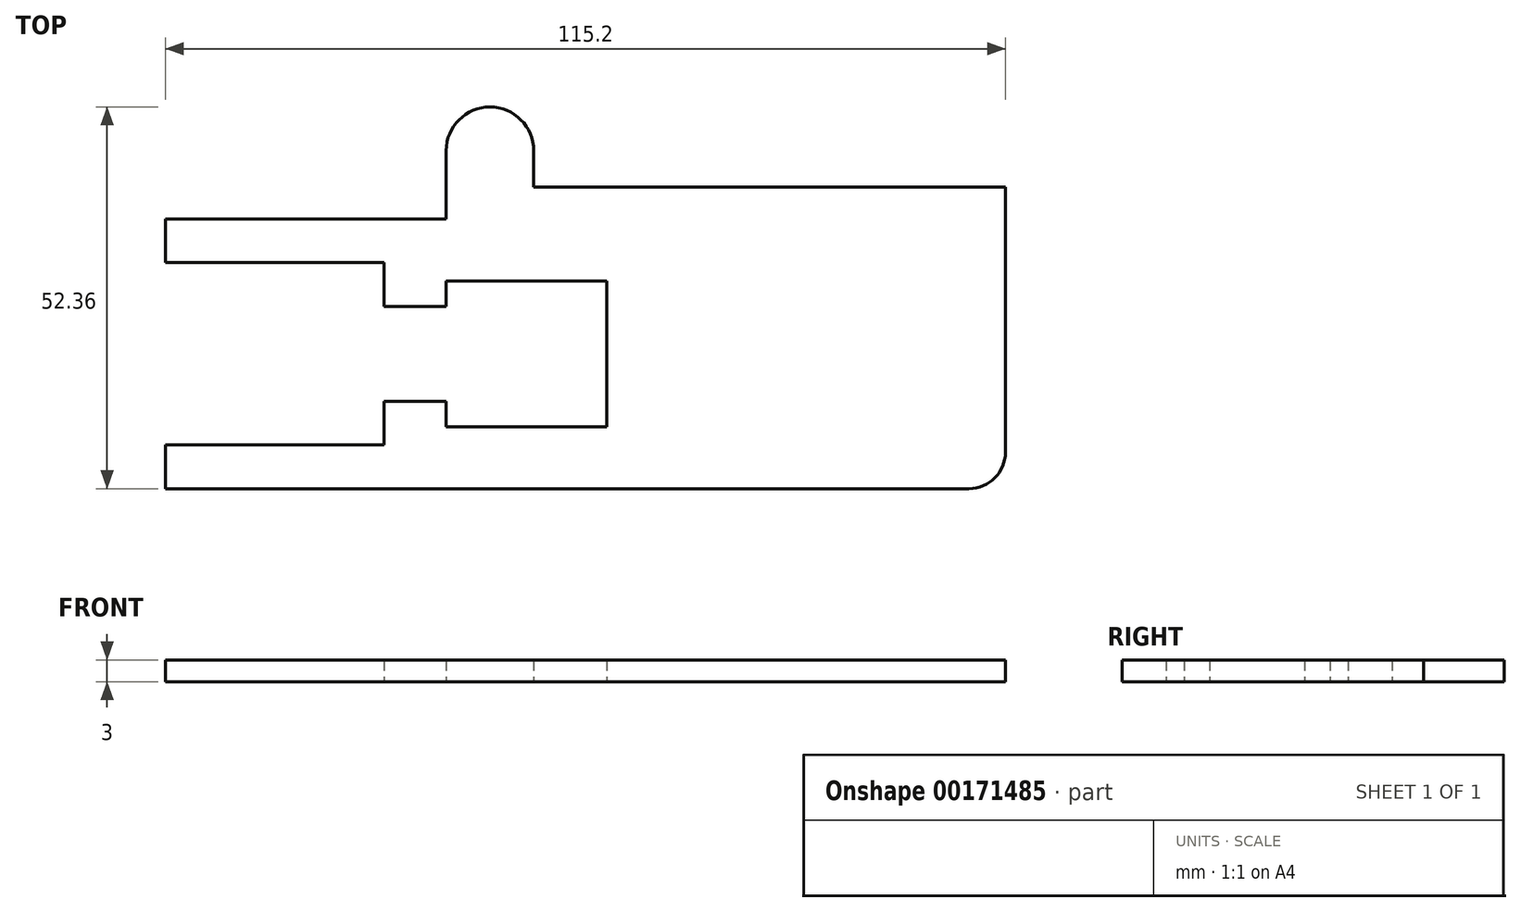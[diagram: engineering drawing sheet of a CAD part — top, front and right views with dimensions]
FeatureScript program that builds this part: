
annotation { "Feature Type Name" : "Feature", "Feature Type Description" : "" }
export const myFeature = defineFeature(function(context is Context, id is Id, definition is map)
    precondition{}
    {
        {
            var Q0;
            Q0=qCreatedBy(makeId("Top.planeOp"),FACE);
            var sketch = newSketch(context, id + "F0", { "sketchPlane" : qUnion([Q0])});
            skLineSegment(sketch, "E0", {"start": v(64.7, 0) * mm, "end": v(64.7, 41.36) * mm});
            skLineSegment(sketch, "E1", {"start": v(64.7, 41.36) * mm, "end": v(0, 41.36) * mm});
            skLineSegment(sketch, "E2", {"start": v(0, 41.36) * mm, "end": v(0, 46.36) * mm});
            skArc(sketch, "E3", {"start": v(0, 46.36) * mm, "mid": v(-6, 52.36) * mm, "end": v(-12, 46.36) * mm});
            skLineSegment(sketch, "E4", {"start": v(-12, 46.36) * mm, "end": v(-12, 37) * mm});
            skLineSegment(sketch, "E5", {"start": v(-12, 37) * mm, "end": v(-50.5, 37) * mm});
            skLineSegment(sketch, "E6", {"start": v(-50.5, 37) * mm, "end": v(-50.5, 31) * mm});
            skLineSegment(sketch, "E7", {"start": v(-50.5, 31) * mm, "end": v(-20.5, 31) * mm});
            skLineSegment(sketch, "E8", {"start": v(-20.5, 31) * mm, "end": v(-20.5, 25) * mm});
            skLineSegment(sketch, "E9", {"start": v(-20.5, 25) * mm, "end": v(-12, 25) * mm});
            skLineSegment(sketch, "E10", {"start": v(-12, 25) * mm, "end": v(-12, 28.5) * mm});
            skLineSegment(sketch, "E11", {"start": v(-12, 28.5) * mm, "end": v(0, 28.5) * mm});
            skLineSegment(sketch, "E12", {"start": v(0, 28.5) * mm, "end": v(10, 28.5) * mm});
            skLineSegment(sketch, "E13", {"start": v(10, 28.5) * mm, "end": v(10, 8.5) * mm});
            skLineSegment(sketch, "E14", {"start": v(10, 8.5) * mm, "end": v(0, 8.5) * mm});
            skLineSegment(sketch, "E15", {"start": v(0, 8.5) * mm, "end": v(-12, 8.5) * mm});
            skLineSegment(sketch, "E16", {"start": v(-12, 8.5) * mm, "end": v(-12, 12) * mm});
            skLineSegment(sketch, "E17", {"start": v(-12, 12) * mm, "end": v(-20.5, 12) * mm});
            skLineSegment(sketch, "E18", {"start": v(-20.5, 12) * mm, "end": v(-20.5, 6) * mm});
            skLineSegment(sketch, "E19", {"start": v(-20.5, 6) * mm, "end": v(-50.5, 6) * mm});
            skLineSegment(sketch, "E20", {"start": v(-50.5, 6) * mm, "end": v(-50.5, 0) * mm});
            skLineSegment(sketch, "E21", {"start": v(-50.5, 0) * mm, "end": v(64.7, 0) * mm});
            skSolve(sketch);
        }
        {
            var Q0;
            Q0=makeQuery(id+"F0.imprint","IMPRINT",FACE,{"disambiguationData":[TD([[makeQuery(id+"F0.imprint","IMPRINT",EDGE,{"derivedFrom":sQuery(id+"F0.wireOp",EDGE,"E0")}),1.0]])]});
            extrude(context, id + "F1", {"entities" : qUnion([Q0]), "depth" : 3 * mm});
        }
        {
            var Q0;
            Q0=makeQuery(id+"F1.opExtrude","SWEPT_EDGE",EDGE,{"disambiguationData":[OSD([sQuery(id+"F0.wireOp",EDGE,"E0"),sQuery(id+"F0.wireOp",EDGE,"E21")])]});
            fillet(context, id + "F2", {"entities" : qUnion([Q0]), "radius" : 5 * mm, "tangentPropagation" : true, "allowEdgeOverflow" : false});
        }
    });
